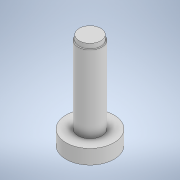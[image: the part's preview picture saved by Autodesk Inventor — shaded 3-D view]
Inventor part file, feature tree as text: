
AUTODESK INVENTOR PART (.ipt)
format: ipt  version: 2020 (Build 240168000, 168)  size: 118,272 bytes
history: native  units: in
note: dims shown in document units (in); Inventor stores cm internally (conversion verified against a paired STEP export)
features: extrude x5, sketch x5
ambient origin geometry x8: Origin, YZ Plane, XZ Plane, XY Plane, X Axis, Y Axis, Z Axis, Center Point
bodies: Solid1 (feature_tree)
feature tree (10):
  extrude  "Extrusion1"  Depth=9.8425in TaperAngle=0.0deg
  extrude  "Extrusion2"  Depth=0.3937in TaperAngle=0.0deg
  extrude  "Extrusion3"  Depth=0.3937in TaperAngle=0.0deg
  extrude  "Extrusion4"  Depth=1.9685in TaperAngle=0.0deg
  extrude  "Extrusion5"  Depth=1.1811in TaperAngle=0.0deg
  sketch  "Sketch1"  dims[d0=1.9685in d1=9.8425in d2=0.0in]
  sketch  "Sketch2"  dims[d3=1.9685in d4=0.3937in d5=0.0in]
  sketch  "Sketch3"  dims[d6=1.7717in d7=0.3937in d8=0.0in]
  sketch  "Sketch4"  dims[d9=1.9685in d10=1.9685in d11=0.0in]
  sketch  "Sketch5"  dims[d12=3.937in d13=1.1811in d14=0.0in]
